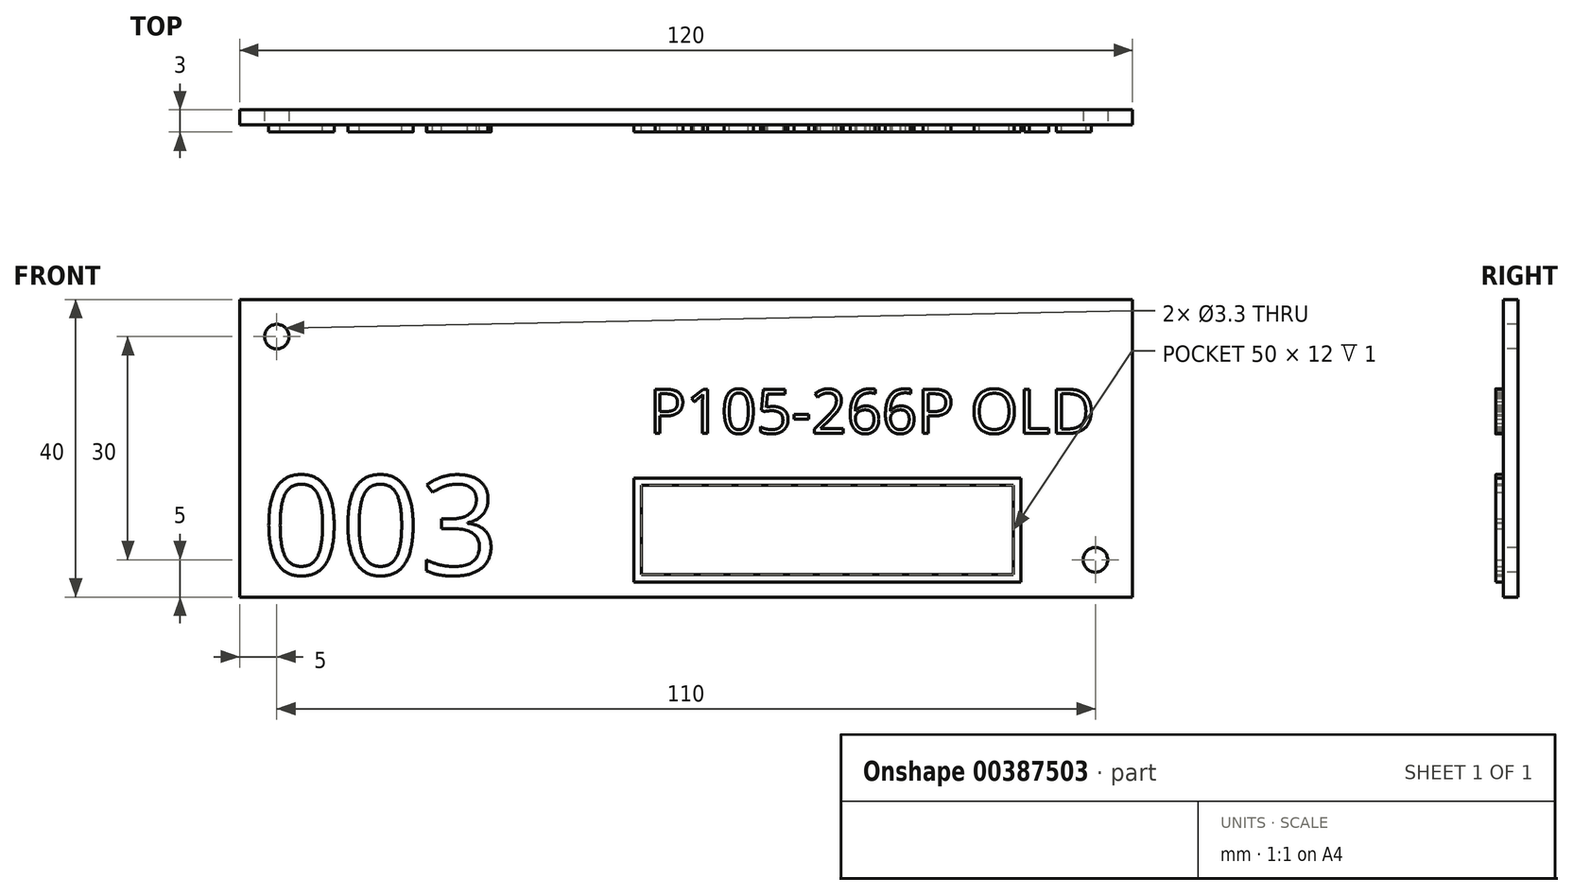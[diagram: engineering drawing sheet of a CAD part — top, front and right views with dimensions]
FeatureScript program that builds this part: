
annotation { "Feature Type Name" : "Feature", "Feature Type Description" : "" }
export const myFeature = defineFeature(function(context is Context, id is Id, definition is map)
    precondition{}
    {
        {
            var Q0;
            Q0=qCreatedBy(makeId("Front.planeOp"),FACE);
            var sketch = newSketch(context, id + "F0", { "sketchPlane" : qUnion([Q0])});
            skLineSegment(sketch, "E0.bottom", {"start": v(60, -20) * mm, "end": v(-60, -20) * mm});
            skLineSegment(sketch, "E0.top", {"start": v(60, 20) * mm, "end": v(-60, 20) * mm});
            skLineSegment(sketch, "E0.left", {"start": v(60, -20) * mm, "end": v(60, 20) * mm});
            skLineSegment(sketch, "E0.right", {"start": v(-60, -20) * mm, "end": v(-60, 20) * mm});
            skPoint(sketch, "E0.middle", {"position": v(0, 0) * mm});
            skSolve(sketch);
        }
        {
            var Q0;
            Q0=makeQuery(id+"F0.imprint","IMPRINT",FACE,{"disambiguationData":[TD([[makeQuery(id+"F0.imprint","IMPRINT",EDGE,{"derivedFrom":sQuery(id+"F0.wireOp",EDGE,"E0.bottom")}),-1.0]])]});
            extrude(context, id + "F1", {"entities" : qUnion([Q0]), "depth" : 2 * mm});
        }
        {
            var Q0;
            Q0=makeQuery(id+"F1.opExtrude","CAP_FACE",FACE,{"disambiguationData":[OSD([sQuery(id+"F0.wireOp",EDGE,"E0.bottom"),sQuery(id+"F0.wireOp",EDGE,"E0.top"),sQuery(id+"F0.wireOp",EDGE,"E0.left"),sQuery(id+"F0.wireOp",EDGE,"E0.right")])],"isStart":false});
            var sketch = newSketch(context, id + "F2", { "sketchPlane" : qUnion([Q0])});
            skPoint(sketch, "E1", {"position": v(-55, 15) * mm});
            skPoint(sketch, "E2", {"position": v(55, -15) * mm});
            skSolve(sketch);
        }
        {
            var Q0;
            Q0=sQuery(id+"F2.wireOp",VERTEX,"E1");
            var Q1;
            Q1=sQuery(id+"F2.wireOp",VERTEX,"E2");
            var Q2;
            Q2=makeQuery(id+"F1.opExtrude","SWEPT_BODY",BODY,{"disambiguationData":[OSD([sQuery(id+"F0.wireOp",EDGE,"E0.bottom"),sQuery(id+"F0.wireOp",EDGE,"E0.top"),sQuery(id+"F0.wireOp",EDGE,"E0.left"),sQuery(id+"F0.wireOp",EDGE,"E0.right")])]});
            hole(context, id + "F3", {"style" : HoleStyle.SIMPLE, "endStyle" : HoleEndStyle.THROUGH, "holeDiameter" : 3.3 * mm, "locations" : qUnion([Q0, Q1]), "scope" : qUnion([Q2]), "isTappedThrough" : true});
        }
        {
            var Q0;
            Q0=makeQuery(id+"F1.opExtrude","CAP_FACE",FACE,{"disambiguationData":[OSD([sQuery(id+"F0.wireOp",EDGE,"E0.bottom"),sQuery(id+"F0.wireOp",EDGE,"E0.top"),sQuery(id+"F0.wireOp",EDGE,"E0.left"),sQuery(id+"F0.wireOp",EDGE,"E0.right")])],"isStart":false});
            var sketch = newSketch(context, id + "F4", { "sketchPlane" : qUnion([Q0])});
            skText(sketch, "E3", { "text": "P105-266P OLD", "fontName": "OpenSans-Regular.ttf"});
            const initialGuessF4  = {"E3": [-0.005, 0.002, 1, 0, 0.00596]};
            skSetInitialGuess(sketch, initialGuessF4);
            skSolve(sketch);
        }
        {
            var Q0;
            Q0=qSketchRegion(id+"F4",true);
            extrude(context, id + "F5", {"entities" : qUnion([Q0]), "operationType" : NewBodyOperationType.ADD, "depth" : 1 * mm});
        }
        {
            var Q0;
            {var subQ0=sQuery(id+"F0.wireOp",EDGE,"E0.top");var subQ1=sQuery(id+"F0.wireOp",EDGE,"E0.left");var subQ2=sQuery(id+"F0.wireOp",EDGE,"E0.right");var subQ3=sQuery(id+"F0.wireOp",EDGE,"E0.bottom");Q0=makeQuery(id+"F5.boolean.opBoolean","SPLIT",FACE,{"disambiguationData":[TD([makeQuery(id+"F1.opExtrude","SWEPT_FACE",FACE,{"disambiguationData":[OSD([subQ3])]})])],"derivedFrom":makeQuery(id+"F1.opExtrude","CAP_FACE",FACE,{"disambiguationData":[OSD([subQ3,subQ0,subQ1,subQ2])],"isStart":false})});}
            var sketch = newSketch(context, id + "F6", { "sketchPlane" : qUnion([Q0])});
            skText(sketch, "E4", { "text": "003", "fontName": "OpenSans-Regular.ttf"});
            const initialGuessF6  = {"E4": [-0.057, -0.017, 1, 0, 0.01338]};
            skSetInitialGuess(sketch, initialGuessF6);
            skSolve(sketch);
        }
        {
            var Q0;
            Q0=qSketchRegion(id+"F6",true);
            extrude(context, id + "F7", {"entities" : qUnion([Q0]), "operationType" : NewBodyOperationType.ADD, "depth" : 1 * mm});
        }
        {
            var Q0;
            {var subQ46=sQuery(id+"F0.wireOp",EDGE,"E0.top");var subQ48=sQuery(id+"F0.wireOp",EDGE,"E0.left");var subQ66=sQuery(id+"F0.wireOp",EDGE,"E0.right");var subQ76=sQuery(id+"F0.wireOp",EDGE,"E0.bottom");var subQ77=makeQuery(id+"F1.opExtrude","SWEPT_FACE",FACE,{"disambiguationData":[OSD([subQ76])]});Q0=makeQuery(id+"F7.boolean.opBoolean","SPLIT",FACE,{"disambiguationData":[TD([subQ77])],"derivedFrom":makeQuery(id+"F5.boolean.opBoolean","SPLIT",FACE,{"disambiguationData":[TD([subQ77])],"derivedFrom":makeQuery(id+"F1.opExtrude","CAP_FACE",FACE,{"disambiguationData":[OSD([subQ76,subQ46,subQ48,subQ66])],"isStart":false})})});}
            var sketch = newSketch(context, id + "F8", { "sketchPlane" : qUnion([Q0])});
            skLineSegment(sketch, "E5.bottom", {"start": v(45, -18) * mm, "end": v(-7, -18) * mm});
            skLineSegment(sketch, "E5.top", {"start": v(45, -4) * mm, "end": v(-7, -4) * mm});
            skLineSegment(sketch, "E5.left", {"start": v(45, -18) * mm, "end": v(45, -4) * mm});
            skLineSegment(sketch, "E5.right", {"start": v(-7, -18) * mm, "end": v(-7, -4) * mm});
            skPoint(sketch, "E5.middle", {"position": v(19, -11) * mm});
            skLineSegment(sketch, "E6.0", {"start": v(44, -5) * mm, "end": v(-6, -5) * mm});
            skLineSegment(sketch, "E6.1", {"start": v(44, -17) * mm, "end": v(44, -5) * mm});
            skLineSegment(sketch, "E6.2", {"start": v(44, -17) * mm, "end": v(-6, -17) * mm});
            skLineSegment(sketch, "E6.3", {"start": v(-6, -17) * mm, "end": v(-6, -5) * mm});
            skSolve(sketch);
        }
        {
            var Q0;
            Q0=makeQuery(id+"F8.imprint","IMPRINT",FACE,{"disambiguationData":[TD([[makeQuery(id+"F8.imprint","IMPRINT",EDGE,{"derivedFrom":sQuery(id+"F8.wireOp",EDGE,"E5.bottom")}),-1.0]])]});
            extrude(context, id + "F9", {"entities" : qUnion([Q0]), "operationType" : NewBodyOperationType.ADD, "depth" : 1 * mm});
        }
    });
